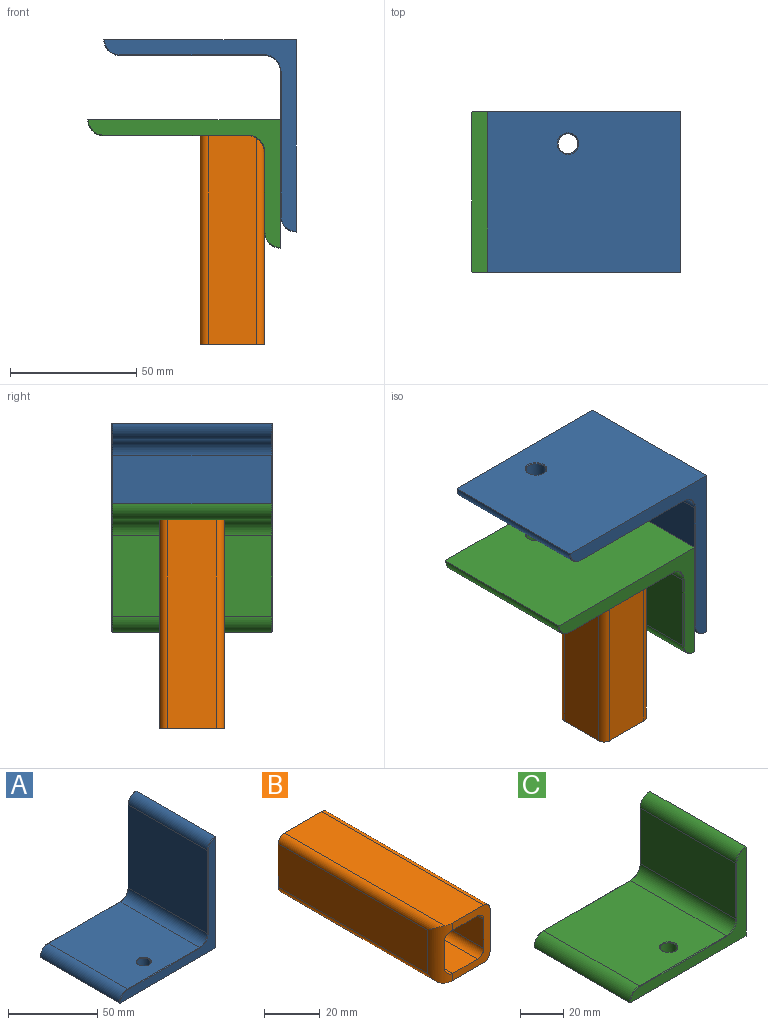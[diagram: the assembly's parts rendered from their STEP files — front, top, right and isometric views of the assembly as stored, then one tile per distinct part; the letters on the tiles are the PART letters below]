
ASSEMBLY  parts=3 mates=2
PART A: 22 faces, bbox 76.2x63.5x76.2 mm
  f0: plane 76.2x63.5mm, normal (1,0,0), area 4838.6mm2, adj f1,f6,f7,f8,f14,f19
  f1: cylinder r=6.35mm len=62.87mm, axis (0,1,0), area 627.1mm2, adj f0,f2,f14,f19
  f2: plane 62.87x57.15mm, normal (-1,0,0), area 3592.7mm2, adj f1,f3,f13,f18
  f3: cylinder r=6.35mm len=62.87mm, axis (0,1,0), area 627.1mm2, adj f2,f4,f12,f17
  f4: plane 62.87x57.15mm, normal (0,0,1), area 3535mm2, adj f3,f5,f11,f16,f20
  f5: cylinder r=6.35mm len=62.87mm, axis (0,1,0), area 627.1mm2, adj f4,f6,f10,f15
  f6: plane 76.2x63.5mm, normal (0,0,-1), area 4780.9mm2, adj f0,f5,f7,f8,f10,f15,f21
  f7: plane 75.88x75.88mm, normal (0,-1,0), area 873.1mm2, adj f0,f6,f15,f16,f17,f18,f19
  f8: plane 75.88x75.88mm, normal (0,1,0), area 873.1mm2, adj f0,f6,f10,f11,f12,f13,f14
  f9: cylinder r=3.97mm len=7.94mm, axis (0,0,-1), area 142.5mm2, adj f20,f21
  f10: cone r=6.35mm half-angle=45deg, axis (0,-1,0), area 4.4mm2, adj f5,f6,f8,f11
  f11: plane 57.15x0.32mm, normal (0,0.71,0.71), area 25.7mm2, adj f4,f8,f10,f12
  f12: cone r=6.67mm half-angle=45deg, axis (0,1,0), area 4.6mm2, adj f3,f8,f11,f13
  f13: plane 57.15x0.32mm, normal (-0.71,0.71,0), area 25.7mm2, adj f2,f8,f12,f14
  f14: cone r=6.35mm half-angle=45deg, axis (0,-1,0), area 4.4mm2, adj f0,f1,f8,f13
  f15: cone r=6.03mm half-angle=45deg, axis (0,1,0), area 4.4mm2, adj f5,f6,f7,f16
  f16: plane 57.15x0.32mm, normal (0,-0.71,0.71), area 25.7mm2, adj f4,f7,f15,f17
  f17: cone r=6.35mm half-angle=45deg, axis (0,-1,0), area 4.6mm2, adj f3,f7,f16,f18
  f18: plane 57.15x0.32mm, normal (-0.71,-0.71,0), area 25.7mm2, adj f2,f7,f17,f19
  f19: cone r=6.03mm half-angle=45deg, axis (0,1,0), area 4.4mm2, adj f0,f1,f7,f18
  f20: cone r=4.29mm half-angle=45deg, axis (0,0,1), area 11.6mm2, adj f4,f9
  f21: cone r=4.29mm half-angle=45deg, axis (0,0,-1), area 11.6mm2, adj f6,f9
PART B: 19 faces, bbox 25.4x82.6x25.4 mm
  f0: cylinder r=3.17mm len=82.55mm, axis (0,1,0), area 411.7mm2, adj f1,f15,f16,f17
  f1: plane 82.55x12.7mm, normal (0,0,1), area 1048.4mm2, adj f0,f2,f16,f17
  f2: cylinder r=3.17mm len=82.55mm, axis (0,1,0), area 409.6mm2, adj f1,f3,f17,f18
  f3: plane 81.7x12.7mm, normal (1,0,0), area 1037.6mm2, adj f2,f4,f17,f18
  f4: cylinder r=3.17mm len=82.55mm, axis (0,1,0), area 409.6mm2, adj f3,f5,f17,f18
  f5: plane 82.55x12.7mm, normal (0,0,-1), area 1048.4mm2, adj f4,f6,f16,f17
  f6: cylinder r=3.17mm len=82.55mm, axis (0,1,0), area 411.7mm2, adj f5,f15,f16,f17
  f7: plane 82.55x19.05mm, normal (0,0,-1), area 1571.7mm2, adj f8,f14,f16,f17,f18
  f8: cylinder r=3.17mm len=82.55mm, axis (0,1,0), area 411.7mm2, adj f7,f9,f16,f17
  f9: plane 82.55x19.05mm, normal (1,0,0), area 1572.6mm2, adj f8,f10,f16,f17
  f10: cylinder r=3.17mm len=82.55mm, axis (0,1,0), area 411.7mm2, adj f9,f11,f16,f17
  f11: plane 82.55x19.05mm, normal (0,0,1), area 1571.7mm2, adj f10,f12,f16,f17,f18
  f12: cylinder r=3.17mm len=81.7mm, axis (0,1,0), area 395.6mm2, adj f11,f13,f17,f18
  f13: plane 76.2x19.05mm, normal (-1,0,0), area 1451.6mm2, adj f12,f14,f17,f18
  f14: cylinder r=3.17mm len=81.7mm, axis (0,1,0), area 395.6mm2, adj f7,f13,f17,f18
  f15: plane 82.55x12.7mm, normal (-1,0,0), area 1048.4mm2, adj f0,f6,f16,f17
  f16: plane 25.4x19.05mm, normal (0,-1,0), area 181.5mm2, adj f0,f1,f5,f6,f7,f8,f9,f10
  f17: plane 25.4x25.4mm, normal (0,1,0), area 282.3mm2, adj f0,f1,f2,f3,f4,f5,f6,f7
  f18: cylinder r=6.35mm len=25.4mm, axis (0,0,1), area 178.8mm2, adj f2,f3,f4,f7,f11,f12,f13,f14
PART C: 22 faces, bbox 76.2x63.5x50.8 mm
  f0: cylinder r=6.35mm len=62.87mm, axis (0,1,0), area 627.1mm2, adj f1,f6,f13,f18
  f1: plane 62.87x57.15mm, normal (0,0,1), area 3535mm2, adj f0,f2,f12,f17,f21
  f2: cylinder r=6.35mm len=62.87mm, axis (0,1,0), area 627.1mm2, adj f1,f3,f11,f16
  f3: plane 76.2x63.5mm, normal (0,0,-1), area 4780.9mm2, adj f2,f4,f7,f8,f10,f11,f16
  f4: plane 63.5x50.8mm, normal (1,0,0), area 3225.7mm2, adj f3,f5,f7,f8,f15,f20
  f5: cylinder r=6.35mm len=62.87mm, axis (0,1,0), area 627.1mm2, adj f4,f6,f15,f20
  f6: plane 62.87x31.75mm, normal (-1,0,0), area 1996mm2, adj f0,f5,f14,f19
  f7: plane 75.88x50.48mm, normal (0,-1,0), area 719.8mm2, adj f3,f4,f11,f12,f13,f14,f15
  f8: plane 75.88x50.48mm, normal (0,1,0), area 719.8mm2, adj f3,f4,f16,f17,f18,f19,f20
  f9: cylinder r=3.97mm len=7.94mm, axis (0,0,-1), area 142.5mm2, adj f10,f21
  f10: cone r=4.29mm half-angle=45deg, axis (0,0,-1), area 11.6mm2, adj f3,f9
  f11: cone r=6.03mm half-angle=45deg, axis (0,1,0), area 4.4mm2, adj f2,f3,f7,f12
  f12: plane 57.15x0.32mm, normal (0,-0.71,0.71), area 25.7mm2, adj f1,f7,f11,f13
  f13: cone r=6.35mm half-angle=45deg, axis (0,-1,0), area 4.6mm2, adj f0,f7,f12,f14
  f14: plane 31.75x0.32mm, normal (-0.71,-0.71,0), area 14.3mm2, adj f6,f7,f13,f15
  f15: cone r=6.03mm half-angle=45deg, axis (0,1,0), area 4.4mm2, adj f4,f5,f7,f14
  f16: cone r=6.35mm half-angle=45deg, axis (0,-1,0), area 4.4mm2, adj f2,f3,f8,f17
  f17: plane 57.15x0.32mm, normal (0,0.71,0.71), area 25.7mm2, adj f1,f8,f16,f18
  f18: cone r=6.67mm half-angle=45deg, axis (0,1,0), area 4.6mm2, adj f0,f8,f17,f19
  f19: plane 31.75x0.32mm, normal (-0.71,0.71,0), area 14.3mm2, adj f6,f8,f18,f20
  f20: cone r=6.35mm half-angle=45deg, axis (0,-1,0), area 4.4mm2, adj f4,f5,f8,f19
  f21: cone r=4.29mm half-angle=45deg, axis (0,0,1), area 11.6mm2, adj f1,f9
PLACE A rot(axis=(-1,0,0),180deg) t=(-11.5,-19.66,101.04)mm
PLACE B rot(axis=(0,-0.71,0.71),180deg) t=(-36.9,-19.66,21.67)mm
PLACE C rot(axis=(-1,0,0),180deg) t=(-17.75,-19.66,69.29)mm
MATE fastened A.f2 <-> C.f4  axis (-1,0,0) through (-17.85,-19.66,31.19)mm
MATE fastened B.f13 <-> C.f6  axis (1,0,0) through (-24.2,-19.66,56.59)mm
